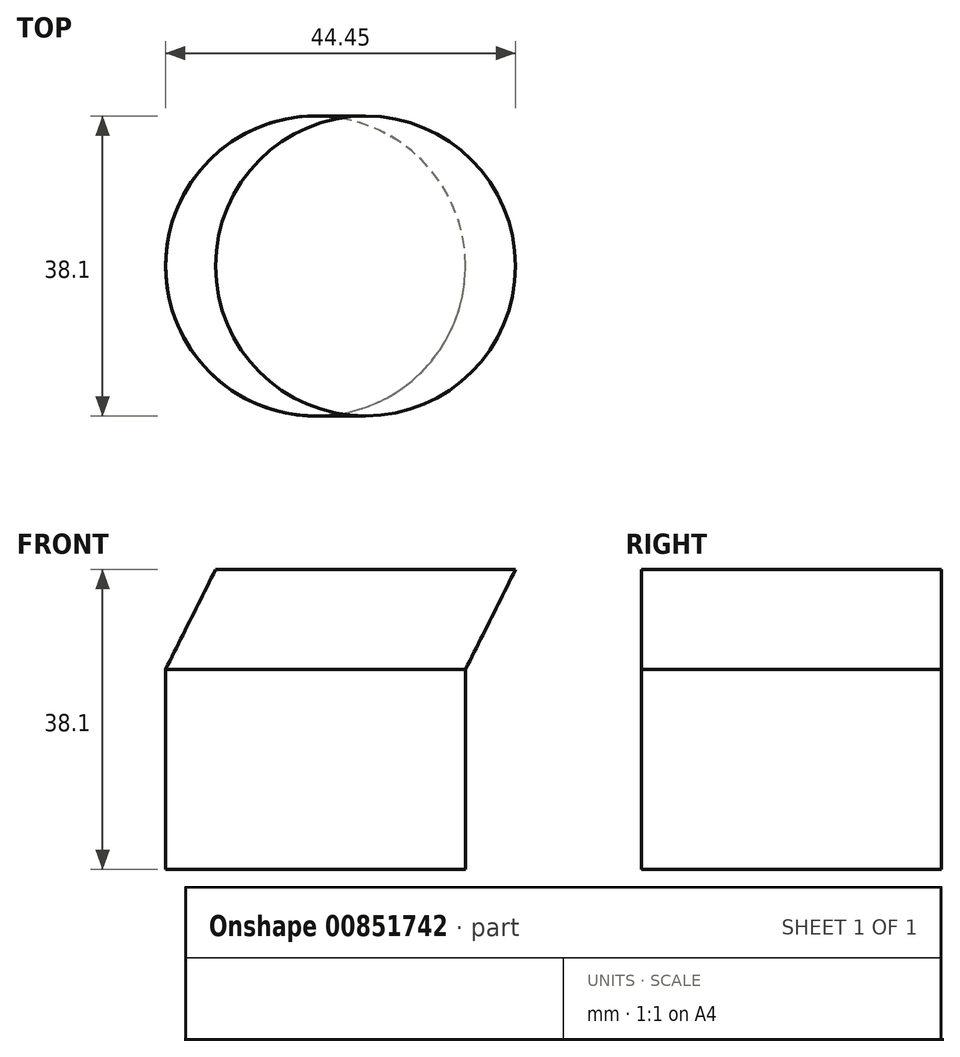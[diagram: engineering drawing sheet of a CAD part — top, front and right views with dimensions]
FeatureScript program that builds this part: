
annotation { "Feature Type Name" : "Feature", "Feature Type Description" : "" }
export const myFeature = defineFeature(function(context is Context, id is Id, definition is map)
    precondition{}
    {
        {
            var Q0;
            Q0=qCreatedBy(makeId("Top.planeOp"),FACE);
            var sketch = newSketch(context, id + "F0", { "sketchPlane" : qUnion([Q0])});
            skCircle(sketch, "E0", {"center": v(0, 0) * mm, "radius": 19.05 * mm});
            skPoint(sketch, "E1", {"position": v(-19.05, 0) * mm});
            skPoint(sketch, "E2", {"position": v(38.1, 0) * mm});
            skSolve(sketch);
        }
        {
            var Q0;
            {var subQ0=sQuery(id+"F0.wireOp",EDGE,"IKvDRBXO-Op61-qvB2-xDeg-EaSQ6AZF5egd");var subQ1=sQuery(id+"F0.wireOp",EDGE,"E0");var subQ2=makeQuery(id+"F0.imprint","INTERSECT",VERTEX,{"disambiguationData":[OD(0.0)],"derivedFrom":[subQ1,subQ0]});Q0=makeQuery(id+"F0.imprint","IMPRINT",FACE,{"disambiguationData":[TD([[makeQuery(id+"F0.imprint","IMPRINT",EDGE,{"disambiguationData":[TD([[subQ2,1.0]])],"derivedFrom":subQ1}),1.0]])]});}
            var Q1;
            {var subQ0=sQuery(id+"F0.wireOp",EDGE,"IKvDRBXO-Op61-qvB2-xDeg-EaSQ6AZF5egd");var subQ1=sQuery(id+"F0.wireOp",EDGE,"E0");var subQ2=makeQuery(id+"F0.imprint","INTERSECT",VERTEX,{"disambiguationData":[OD(0.0)],"derivedFrom":[subQ1,subQ0]});Q1=makeQuery(id+"F0.imprint","IMPRINT",FACE,{"disambiguationData":[TD([[makeQuery(id+"F0.imprint","IMPRINT",EDGE,{"disambiguationData":[TD([[subQ2,-1.0]])],"derivedFrom":subQ1}),1.0]])]});}
            extrude(context, id + "F1", {"entities" : qUnion([Q0, Q1]), "depth" : 25.4 * mm, "offsetDistance" : 25.4 * mm});
        }
        {
            var Q0;
            Q0=makeQuery(id+"F1.opExtrude","CAP_FACE",FACE,{"disambiguationData":[OSD([sQuery(id+"F0.wireOp",EDGE,"E0")])],"isStart":false});
            cPlane(context, id + "F2", {"entities" : qUnion([Q0]), "cplaneType" : CPlaneType.OFFSET, "offset" : 12.7 * mm, "width" : 152.4 * mm, "height" : 152.4 * mm});
        }
        {
            var Q0;
            Q0=qCreatedBy(id+"F2.planeOp",FACE);
            var sketch = newSketch(context, id + "F3", { "sketchPlane" : qUnion([Q0])});
            skCircle(sketch, "E3.0", {"center": v(6.35, 0) * mm, "radius": 19.05 * mm});
            skPoint(sketch, "E4", {"position": v(0, 0) * mm});
            skPoint(sketch, "E5", {"position": v(25.4, 0) * mm});
            skLineSegment(sketch, "E6", {"start": v(0, 0) * mm, "end": v(25.4, 0) * mm, "construction": true});
            skPoint(sketch, "E7.0", {"position": v(-19.05, 0) * mm});
            skPoint(sketch, "E8", {"position": v(-12.7, 0) * mm});
            skSolve(sketch);
        }
        {
            var Q0;
            Q0=makeQuery(id+"F1.opExtrude","CAP_FACE",FACE,{"disambiguationData":[OSD([sQuery(id+"F0.wireOp",EDGE,"E0")])],"isStart":false});
            var sketch = newSketch(context, id + "F4", { "sketchPlane" : qUnion([Q0])});
            skPoint(sketch, "E9.0", {"position": v(-19.05, 0) * mm});
            skPoint(sketch, "E10", {"position": v(19.05, 0) * mm});
            skSolve(sketch);
        }
        {
            var Q0;
            Q0=sQuery(id+"F3.wireOp",EDGE,"E6");
            var Q1;
            Q1=qCreatedBy(id+"F2.planeOp",FACE);
            cPlane(context, id + "F5", {"entities" : qUnion([Q0, Q1]), "cplaneType" : CPlaneType.LINE_ANGLE, "offset" : 25.4 * mm, "angle" : 90 * degree, "width" : 152.4 * mm, "height" : 152.4 * mm});
        }
        {
            var Q0;
            Q0=qCreatedBy(id+"F5.planeOp",FACE);
            var sketch = newSketch(context, id + "F6", { "sketchPlane" : qUnion([Q0])});
            skPoint(sketch, "E11.0", {"position": v(-25.4, 38.1) * mm});
            skPoint(sketch, "E12.0", {"position": v(19.05, 25.4) * mm});
            skPoint(sketch, "E13.0", {"position": v(-19.05, 25.4) * mm});
            skLineSegment(sketch, "E14", {"start": v(-25.4, 38.1) * mm, "end": v(-19.05, 25.4) * mm});
            skPoint(sketch, "E15.0", {"position": v(12.7, 38.1) * mm});
            skLineSegment(sketch, "E16", {"start": v(12.7, 38.1) * mm, "end": v(19.05, 25.4) * mm});
            skSolve(sketch);
        }
        {
            var Q0;
            Q0=makeQuery(id+"F4.imprint","IMPRINT",FACE,{"disambiguationData":[TD([[makeQuery(id+"F4.imprint","IMPRINT",EDGE,{"derivedFrom":makeQuery(id+"F1.opExtrude","CAP_EDGE",EDGE,{"disambiguationData":[OSD([sQuery(id+"F0.wireOp",EDGE,"E0")])],"isStart":false})}),1.0]])]});
            var Q1;
            Q1=makeQuery(id+"F3.imprint","IMPRINT",FACE,{"disambiguationData":[TD([[makeQuery(id+"F3.imprint","IMPRINT",EDGE,{"derivedFrom":sQuery(id+"F3.wireOp",EDGE,"E3.0")}),1.0]])]});
            var Q2;
            Q2=sQuery(id+"F6.wireOp",EDGE,"0mM5FJKJ-lpxl-R0XP-4Ja7-eDmrkPlbok2s");
            var Q3;
            Q3=sQuery(id+"F6.wireOp",EDGE,"E14");
            loft(context, id + "F7", {"addGuides" : true, "sheetProfilesArray" : [{ "sheetProfileEntities" : qUnion([Q0]) }, { "sheetProfileEntities" : qUnion([Q1]) }], "guidesArray" : [{ "guideEntities" : qUnion([Q2]), "guideDerivativeType" : LoftGuideDerivativeType.DEFAULT, "guideDerivativeMagnitude" : 1 }, { "guideEntities" : qUnion([Q3]), "guideDerivativeType" : LoftGuideDerivativeType.DEFAULT, "guideDerivativeMagnitude" : 1 }]});
        }
    });
